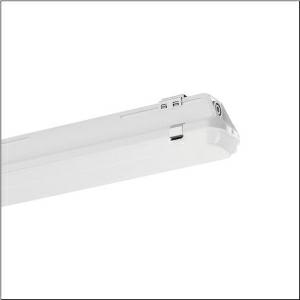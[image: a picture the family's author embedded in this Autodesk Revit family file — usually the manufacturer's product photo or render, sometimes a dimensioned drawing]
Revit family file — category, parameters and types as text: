
# Revit family: monsun_r__21_51fb207p480c_6d06
name_source: partatom
category: Lighting Fixtures
units: mm (PartAtom-declared; Revit-internal decimal feet)

## family parameters
Cut with Voids When Loaded = No
Host = Face
Light Source = No
Part Type = Normal
Room Calculation Point = No
Round Connector Dimension = Use Diameter
Shared = No

## types (1)
- Monsun® 21 (1 x LED, 7270 lm, 44.5 W, 4000K)
    Apparent Load = 45 VA
    CIE Flux Codes = 45 75 93 94 100
    Color Rendering = 80
    Color Temperature = 4000K
    Default Elevation = 1800 mm
    Description = Monsun® 21, damp-proof luminaire, chain hanger, primary optical cover: enclosure, of PC, light emission: direct distribution, primary light characteristic: symmetric, installation type: suspended mounting, surface-mounted, horizontal mounting, vertical mounting, LED, rated luminous flux: 7.270lm, luminous efficacy: 163lm/W, light colour: 840, colour temperature: 4000K, control gear: ON/OFF, with terminal, 3-pole, max. 2.5mm², mains connection: 220..240V, AC, 50/60Hz, rated input power: 45W, housing, of glass-fibre reinforced polyester, uncoated, bright grey, incl. chain hanger, length: 1.590mm, width: 90mm, height: 88mm, clip for enclosure, of stainless steel (V2A), ceiling mounting element, of stainless steel (V2A), chain hanger, of stainless steel (V2A), protection rating (complete): IP66, insulation class (complete): insulation class I (protective earthing), certification: CE, ENEC, VDE, UKCA, protection symbol: D, impact resistance: IK08, permissible operating ambient temperature: -25..+35°C, standard: EN 50419, EN 60598-2-1, corresponds to IFS (International Featured Standards) requirements for safety and quality in the food industry, for indoor or canopied outdoor use, no direct snow, no direct sun, no direct rain, LABS conformity tested according to VDMA 24364:2018-05, contact your sales advisor before using the luminaires in applications with unclear chemical exposure, large temperature fluctuations or condensation-forming humidity, packaging unit: 1 piece
    Height = 89 mm
    Lamp = 1 x LED
    Lamp Light Flux = 7270 lm
    Lamp Power = 44.5 W
    Lamp count = 1
    Length = 1590 mm
    Luminous efficacy = 163 lm/W
    Manufacturer = Siteco
    ModVariant = No
    Model = 51FB207P480C
    Mounting Place = Ceiling
    Mounting Type = Surface mounted
    Number of Poles = 1
    OnlyDefault = Yes
    Power Factor = 1
    Product Name = Monsun® 21
    Product group = damp-proof luminaire
    ProductGroupID = 301
    Protection Class = Protection class I
    Protection Degree = IP 66
    RLX_Detail_Level = 1
    RLX_Emergency_Light_Flux = 0 lm
    RLX_Emergency_Type = 0
    RLX_Emergency_Type_DB = No
    RlxData = <blob elided: 88429 chars, md5=d0ef3120>
    Socket = socket
    Standby Power = 0 W
    System Light Flux = 7270 lm
    System Power = 45 W
    Type Comments = Product without accessories
    Type Image = l_1319656.jpg
    URL = http://relux.com
    VarID = ---
    Voltage = 0 V
    Weight = 0.00 kg
    Width = 90 mm

## geometry (parser evidence)
native form markers: Blend x4, Sweep x12
no freeform markers — native parametric forms only
